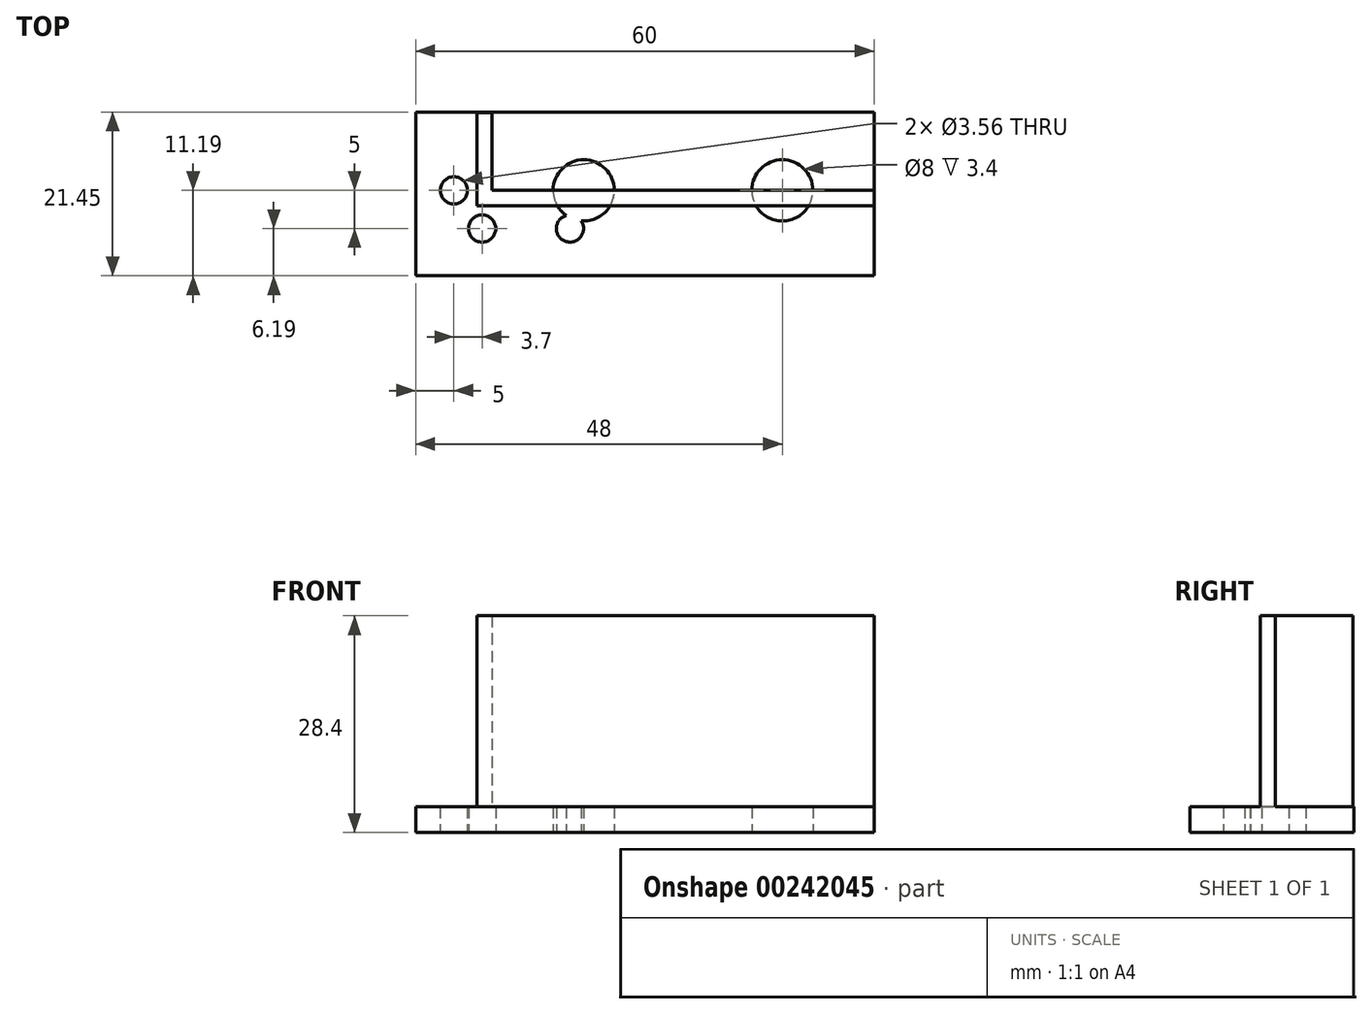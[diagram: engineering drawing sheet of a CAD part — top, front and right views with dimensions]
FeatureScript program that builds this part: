
annotation { "Feature Type Name" : "Feature", "Feature Type Description" : "" }
export const myFeature = defineFeature(function(context is Context, id is Id, definition is map)
    precondition{}
    {
        {
            var Q0;
            Q0=qCreatedBy(makeId("Top.planeOp"),FACE);
            var sketch = newSketch(context, id + "F0", { "sketchPlane" : qUnion([Q0])});
            skLineSegment(sketch, "E0.bottom", {"start": v(0, 0) * mm, "end": v(50, 0) * mm, "construction": true});
            skLineSegment(sketch, "E0.top", {"start": v(0, 80) * mm, "end": v(50, 80) * mm, "construction": true});
            skLineSegment(sketch, "E0.left", {"start": v(0, 0) * mm, "end": v(0, 80) * mm, "construction": true});
            skLineSegment(sketch, "E0.right", {"start": v(50, 0) * mm, "end": v(50, 80) * mm, "construction": true});
            skLineSegment(sketch, "E1", {"start": v(0, 10.26) * mm, "end": v(-10, 10.26) * mm});
            skLineSegment(sketch, "E2", {"start": v(-10, 10.26) * mm, "end": v(-10, -11.2) * mm});
            skLineSegment(sketch, "E3", {"start": v(-10, -11.2) * mm, "end": v(50, -11.2) * mm});
            skLineSegment(sketch, "E4", {"start": v(50, -11.2) * mm, "end": v(50, 0) * mm});
            skLineSegment(sketch, "E5", {"start": v(50, 0) * mm, "end": v(0, 0) * mm});
            skLineSegment(sketch, "E6", {"start": v(0, 10.26) * mm, "end": v(50, 10.26) * mm});
            skLineSegment(sketch, "E7", {"start": v(50, 10.26) * mm, "end": v(50, 0) * mm});
            skCircle(sketch, "E8", {"center": v(12, 0) * mm, "radius": 4 * mm});
            skLineSegment(sketch, "E9", {"start": v(25, 0) * mm, "end": v(25, 23.83) * mm, "construction": true});
            skPoint(sketch, "E9.endSnap0", {"position": v(25, 10.26) * mm});
            skCircle(sketch, "E10.MirrorC", {"center": v(38, 0) * mm, "radius": 4 * mm});
            skCircle(sketch, "E11", {"center": v(-5, 0) * mm, "radius": 1.78 * mm});
            skCircle(sketch, "E12", {"center": v(-1.3, -5) * mm, "radius": 1.78 * mm});
            skCircle(sketch, "E13.1.0.0", {"center": v(10.2, -5) * mm, "radius": 1.78 * mm});
            skLineSegment(sketch, "E13.direction1", {"start": v(-1.3, -5) * mm, "end": v(10.2, -5) * mm, "construction": true});
            skSolve(sketch);
        }
        {
            var Q0;
            Q0 = qSketchRegion(id + "F0", true);
            extrude(context, id + "F1", {"entities" : qUnion([Q0]), "depth" : 3.4 * mm});
        }
        {
            var Q0;
            Q0=makeQuery(id+"F1.opExtrude","CAP_FACE",FACE,{"disambiguationData":[OSD([sQuery(id+"F0.wireOp",EDGE,"E1"),sQuery(id+"F0.wireOp",EDGE,"E2"),sQuery(id+"F0.wireOp",EDGE,"E3"),sQuery(id+"F0.wireOp",EDGE,"E4"),sQuery(id+"F0.wireOp",EDGE,"E6"),sQuery(id+"F0.wireOp",EDGE,"E7"),sQuery(id+"F0.wireOp",EDGE,"E8"),sQuery(id+"F0.wireOp",EDGE,"E10.MirrorC"),sQuery(id+"F0.wireOp",EDGE,"E11"),sQuery(id+"F0.wireOp",EDGE,"E12"),sQuery(id+"F0.wireOp",EDGE,"E13.1.0.0")])],"isStart":false});
            var sketch = newSketch(context, id + "F2", { "sketchPlane" : qUnion([Q0])});
            skSolve(sketch);
        }
        {
            var Q0;
            Q0=makeQuery(id+"F2.imprint","IMPRINT",FACE,{"disambiguationData":[TD([[makeQuery(id+"F2.imprint","IMPRINT",EDGE,{"derivedFrom":makeQuery(id+"F1.opExtrude","CAP_EDGE",EDGE,{"disambiguationData":[OSD([sQuery(id+"F0.wireOp",EDGE,"E2")])],"isStart":false})}),1.0]])]});
            var sketch = newSketch(context, id + "F3", { "sketchPlane" : qUnion([Q0])});
            skLineSegment(sketch, "E14", {"start": v(0, 0) * mm, "end": v(0, 10.18) * mm});
            skLineSegment(sketch, "E15", {"start": v(0, 10.18) * mm, "end": v(-2, 10.18) * mm});
            skLineSegment(sketch, "E16", {"start": v(-2, 10.18) * mm, "end": v(-2, -2) * mm});
            skLineSegment(sketch, "E17", {"start": v(-2, -2) * mm, "end": v(50, -2) * mm});
            skLineSegment(sketch, "E18", {"start": v(50, -2) * mm, "end": v(50, 0) * mm});
            skLineSegment(sketch, "E19", {"start": v(50, 0) * mm, "end": v(0, 0) * mm});
            skSolve(sketch);
        }
        {
            var Q0;
            Q0 = qSketchRegion(id + "F3", true);
            extrude(context, id + "F4", {"entities" : qUnion([Q0]), "operationType" : NewBodyOperationType.ADD, "depth" : 25 * mm});
        }
    });
